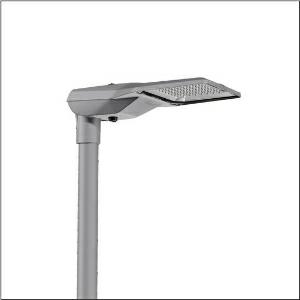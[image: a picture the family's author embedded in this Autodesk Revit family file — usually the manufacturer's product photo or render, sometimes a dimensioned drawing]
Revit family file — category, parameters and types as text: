
# Revit family: streetlight_sl_21_midi___st0_5a_5xe3b43t08mb_3943
name_source: partatom
category: Lighting Fixtures
units: mm (PartAtom-declared; Revit-internal decimal feet)

## family parameters
Cut with Voids When Loaded = No
Host = Face
Light Source = No
Part Type = Normal
Room Calculation Point = No
Round Connector Dimension = Use Diameter
Shared = No

## types (1)
- --- (1 x LED, 20180 lm, 147 W, 4000K)
    Apparent Load = 147 VA
    CIE Flux Codes = 41 75 97 100 100
    Color Rendering = 70
    Color Temperature = 4000K
    Default Elevation = 1800 mm
    Description = Streetlight SL 21 midi, mast luminaire, primary light control with lens, of PMMA, primary optical cover: cover, of toughened safety glass, transparent, light distribution: ST0.5a, light emission: direct distribution, primary light characteristic: asymmetric, installation type: side-entry, post-top, LED, High Power LED, rated luminous flux: 20.180lm, luminous efficacy: 137lm/W, light colour: 740, colour temperature: 4000K, control gear: D4i, control: overheat protection, constant luminous flux control, time-dependent luminous flux control, flexible luminous flux parameterisation, pre-setting: logarithmic dimming characteristic, mains connection: 230..240V, AC, 50/60Hz, start of lifetime: 147W, end of service life: 155W, reduction: 65W, luminaire housing, of diecast aluminium, powder-coated, Siteco® metallic grey (DB 702S), corrosivity category C5 mid according to DIN EN ISO 12944, please order mast flange separately, inclination adjustable: 0°, 5°, 10°, 15°, sealing non-destructively replaceable, multi-level sealing system, length: 644mm, width: 335mm, height: 110mm, mast flange for spigot size: 42mm (side-entry): 5XC10008XM4, 60/48mm (side-entry/post-top): 5XC10108XM2, 76/60mm (side-entry/post-top): 5XC10108XM1, mounting height: 4..8m, Smart Interface below and above, protection rating (complete): IP66, insulation class (complete): insulation class II (safety insulation), certification: CE, ENEC, ENEC+, VDE, impact resistance: IK10, permissible operating ambient temperature for outdoor applications: -40..+50°C, standard-compliant lighting for roads and squares, packaging unit: 1 piece

Light Distribution: ST0.5a
    Height = 111 mm
    Lamp = 1 x LED
    Lamp Light Flux = 20180 lm
    Lamp Power = 147 W
    Lamp count = 1
    Length = 644 mm
    Luminous efficacy = 137 lm/W
    Manufacturer = Siteco
    ModVariant = No
    Model = 5XE3B43T08MB
    Number of Poles = 1
    OnlyDefault = Yes
    Power Factor = 1
    Product Name = Streetlight SL 21 midi | ST0.5a
    Product group = mast luminaire | pylon top
    ProductGroupID = 6100
    Protection Class = Protection class II
    Protection Degree = IP 66
    RLX_Detail_Level = 1
    RLX_Emergency_Light_Flux = 0 lm
    RLX_Emergency_Type = 0
    RLX_Emergency_Type_DB = No
    RlxData = <blob elided: 38029 chars, md5=5bbe79ed>
    Socket = socket
    Standby Power = 0 W
    System Light Flux = 20180 lm
    System Power = 147 W
    Type Comments = factory setting: luminous flux: 100 % | dim-lin: 254 | 750 mA
    Type Image = l_1004304.jpg
    URL = http://relux.com
    VarID = @adj_191606
    Voltage = 0 V
    Weight = 0.00 kg
    Width = 336 mm

## geometry (parser evidence)
native form markers: Blend x4, Sweep x11
no freeform markers — native parametric forms only
